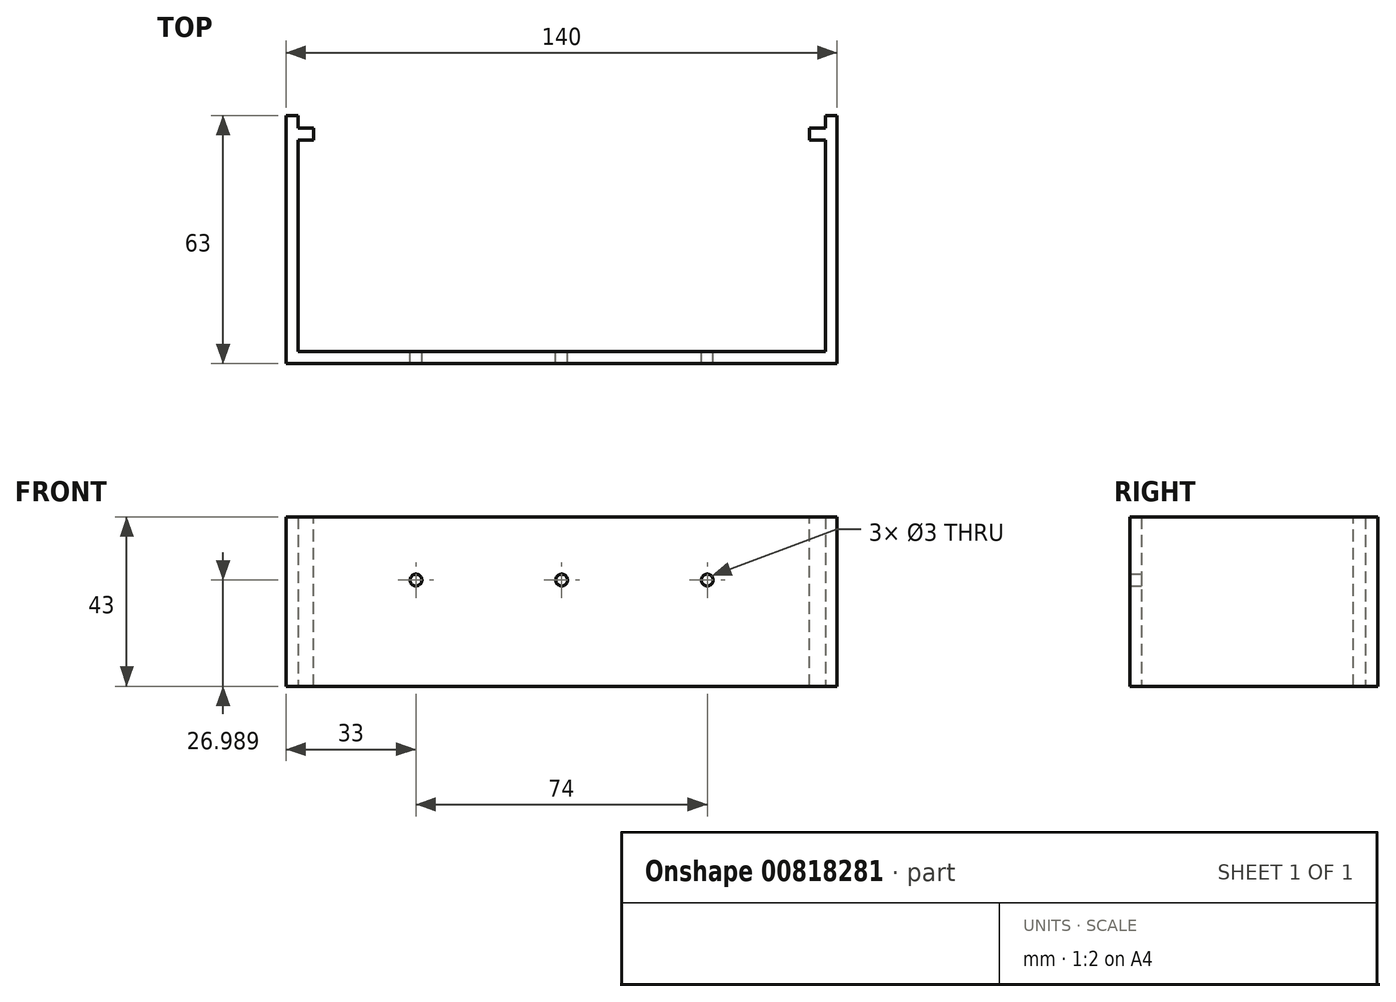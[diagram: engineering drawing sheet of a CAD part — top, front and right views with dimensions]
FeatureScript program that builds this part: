
annotation { "Feature Type Name" : "Feature", "Feature Type Description" : "" }
export const myFeature = defineFeature(function(context is Context, id is Id, definition is map)
    precondition{}
    {
        {
            var Q0;
            Q0=qCreatedBy(makeId("Top.planeOp"),FACE);
            var sketch = newSketch(context, id + "F0", { "sketchPlane" : qUnion([Q0])});
            skLineSegment(sketch, "E0.bottom", {"start": v(-80, 33.03) * mm, "end": v(60, 33.03) * mm});
            skLineSegment(sketch, "E0.top", {"start": v(-80, -32.97) * mm, "end": v(60, -32.97) * mm});
            skLineSegment(sketch, "E0.left", {"start": v(-80, 33.03) * mm, "end": v(-80, -32.97) * mm});
            skLineSegment(sketch, "E0.right", {"start": v(60, 33.03) * mm, "end": v(60, -32.97) * mm});
            skLineSegment(sketch, "E1.left", {"start": v(-80, -32.97) * mm, "end": v(-80, 0.03) * mm});
            skLineSegment(sketch, "E1.right", {"start": v(60, -9.97) * mm, "end": v(60, 0.03) * mm});
            skLineSegment(sketch, "E2.bottom", {"start": v(-80, -32.97) * mm, "end": v(-45, -32.97) * mm});
            skLineSegment(sketch, "E2.top", {"start": v(-80, 33.03) * mm, "end": v(-60, 33.03) * mm});
            skLineSegment(sketch, "E2.left", {"start": v(-80, -32.97) * mm, "end": v(-80, 33.03) * mm});
            skLineSegment(sketch, "E3.bottom", {"start": v(-45, -32.97) * mm, "end": v(-25, -32.97) * mm});
            skLineSegment(sketch, "E3.top", {"start": v(-60, 33.03) * mm, "end": v(-40, 33.03) * mm});
            skLineSegment(sketch, "E4.bottom", {"start": v(-25, -32.97) * mm, "end": v(-5, -32.97) * mm});
            skLineSegment(sketch, "E4.top", {"start": v(-40, 33.03) * mm, "end": v(-20, 33.03) * mm});
            skPoint(sketch, "E5.oppositeSnap0", {"position": v(-10, 33.03) * mm});
            skLineSegment(sketch, "E5.bottom", {"start": v(-5, -32.97) * mm, "end": v(15, -32.97) * mm});
            skLineSegment(sketch, "E5.top", {"start": v(-20, 33.03) * mm, "end": v(0, 33.03) * mm});
            skLineSegment(sketch, "E6.bottom", {"start": v(15, -32.97) * mm, "end": v(35, -32.97) * mm});
            skLineSegment(sketch, "E6.top", {"start": v(0, 33.03) * mm, "end": v(20, 33.03) * mm});
            skLineSegment(sketch, "E7.bottom", {"start": v(35, -32.97) * mm, "end": v(55, -32.97) * mm});
            skLineSegment(sketch, "E7.top", {"start": v(20, 33.03) * mm, "end": v(40, 33.03) * mm});
            skLineSegment(sketch, "E8.left", {"start": v(-80, -32.97) * mm, "end": v(-80, -2.97) * mm});
            skLineSegment(sketch, "E8.right", {"start": v(60, -24.97) * mm, "end": v(60, -4.97) * mm});
            skLineSegment(sketch, "E9.left", {"start": v(-80, 33.03) * mm, "end": v(-80, 18.03) * mm});
            skLineSegment(sketch, "E9.right", {"start": v(60, 33.03) * mm, "end": v(60, 18.03) * mm});
            skCircle(sketch, "E10", {"center": v(-45, 1.03) * mm, "radius": 8 * mm});
            skCircle(sketch, "E11", {"center": v(25, -0.47) * mm, "radius": 8 * mm});
            skLineSegment(sketch, "E12.left", {"start": v(-80, -32.97) * mm, "end": v(-80, -17.97) * mm});
            skLineSegment(sketch, "E12.right", {"start": v(60, -32.97) * mm, "end": v(60, -14.97) * mm});
            skLineSegment(sketch, "E13.top", {"start": v(-80, -29.97) * mm, "end": v(60, -29.97) * mm});
            skLineSegment(sketch, "E13.left", {"start": v(-80, -32.97) * mm, "end": v(-80, -29.97) * mm});
            skLineSegment(sketch, "E13.right", {"start": v(60, -32.97) * mm, "end": v(60, -29.97) * mm});
            skSolve(sketch);
        }
        {
            var Q0;
            Q0=makeQuery(id+"F0.imprint","IMPRINT",FACE,{"disambiguationData":[TD([[makeQuery(id+"F0.imprint","IMPRINT",EDGE,{"derivedFrom":sQuery(id+"F0.wireOp",EDGE,"E0.right")}),-1.0]])]});
            extrude(context, id + "F1", {"entities" : qUnion([Q0]), "depth" : 3 * mm, "offsetDistance" : 25 * mm});
        }
        {
            var Q0;
            Q0=makeQuery(id+"F1.opExtrude","CAP_FACE",FACE,{"disambiguationData":[OSD([sQuery(id+"F0.wireOp",EDGE,"E0.right"),sQuery(id+"F0.wireOp",EDGE,"E1.right"),sQuery(id+"F0.wireOp",EDGE,"E2.left"),sQuery(id+"F0.wireOp",EDGE,"E8.left"),sQuery(id+"F0.wireOp",EDGE,"E8.right"),sQuery(id+"F0.wireOp",EDGE,"E0.bottom"),sQuery(id+"F0.wireOp",EDGE,"E9.left"),sQuery(id+"F0.wireOp",EDGE,"E9.right"),sQuery(id+"F0.wireOp",EDGE,"l78r6zbi-zdNL-ogfi-jeJ1-84AOC1EXPDmI"),sQuery(id+"F0.wireOp",EDGE,"7xFXzIXv-dOzj-SHI9-m5NP-5MGqcVb28G0k"),sQuery(id+"F0.wireOp",EDGE,"E10"),sQuery(id+"F0.wireOp",EDGE,"k8Uu2vQ0-tXef-bBox-vRSx-lKBiwxJhI1xb"),sQuery(id+"F0.wireOp",EDGE,"E11"),sQuery(id+"F0.wireOp",EDGE,"5OqNOj1d-C8S8-WuIc-Ppvz-3VOTpNMQOR2k"),sQuery(id+"F0.wireOp",EDGE,"E12.left"),sQuery(id+"F0.wireOp",EDGE,"E12.right"),sQuery(id+"F0.wireOp",EDGE,"HoM0chx2-d7kJ-X9MT-WdqG-gqhH9dmnozYe"),sQuery(id+"F0.wireOp",EDGE,"JgkcrWLJ-2lYI-B5tP-8zwM-9y0SQbQCKJUD"),sQuery(id+"F0.wireOp",EDGE,"uQcqgJcq-6ofs-f9DD-1k3D-WOd607GN4n9v"),sQuery(id+"F0.wireOp",EDGE,"E13.top")])],"isStart":false});
            var sketch = newSketch(context, id + "F2", { "sketchPlane" : qUnion([Q0])});
            skLineSegment(sketch, "E14.bottom", {"start": v(-80, -29.97) * mm, "end": v(60, -29.97) * mm});
            skLineSegment(sketch, "E14.top", {"start": v(-80, -26.97) * mm, "end": v(60, -26.97) * mm});
            skLineSegment(sketch, "E14.left", {"start": v(-80, -29.97) * mm, "end": v(-80, -26.97) * mm});
            skLineSegment(sketch, "E14.right", {"start": v(60, -29.97) * mm, "end": v(60, -26.97) * mm});
            skLineSegment(sketch, "E15.left", {"start": v(-80, 33.03) * mm, "end": v(-80, 30.03) * mm});
            skLineSegment(sketch, "E15.right", {"start": v(60, 33.03) * mm, "end": v(60, 30.03) * mm});
            skLineSegment(sketch, "E16.bottom", {"start": v(-80, 33.03) * mm, "end": v(-77, 33.03) * mm});
            skLineSegment(sketch, "E16.top", {"start": v(-80, -29.97) * mm, "end": v(-77, -29.97) * mm});
            skLineSegment(sketch, "E16.left", {"start": v(-80, 33.03) * mm, "end": v(-80, -29.97) * mm});
            skLineSegment(sketch, "E16.right", {"start": v(-77, 33.03) * mm, "end": v(-77, -29.97) * mm});
            skLineSegment(sketch, "E17.bottom", {"start": v(60, 33.03) * mm, "end": v(57, 33.03) * mm});
            skLineSegment(sketch, "E17.top", {"start": v(60, -29.97) * mm, "end": v(57, -29.97) * mm});
            skLineSegment(sketch, "E17.left", {"start": v(60, 33.03) * mm, "end": v(60, -29.97) * mm});
            skLineSegment(sketch, "E17.right", {"start": v(57, 33.03) * mm, "end": v(57, -29.97) * mm});
            skSolve(sketch);
        }
        {
            var Q0;
            Q0=qSketchRegion(id+"F2",true);
            extrude(context, id + "F3", {"entities" : qUnion([Q0]), "operationType" : NewBodyOperationType.ADD, "depth" : 40 * mm, "offsetDistance" : 25 * mm});
        }
        {
            var Q0;
            Q0=makeQuery(id+"F3.opExtrude","SWEPT_FACE",FACE,{"disambiguationData":[OSD([sQuery(id+"F2.wireOp",EDGE,"E16.right")])]});
            var sketch = newSketch(context, id + "F4", { "sketchPlane" : qUnion([Q0])});
            skLineSegment(sketch, "E18.bottom", {"start": v(33.03, 43) * mm, "end": v(29.83, 43) * mm});
            skLineSegment(sketch, "E18.top", {"start": v(33.03, 3) * mm, "end": v(29.83, 3) * mm});
            skLineSegment(sketch, "E18.left", {"start": v(33.03, 43) * mm, "end": v(33.03, 3) * mm});
            skLineSegment(sketch, "E18.right", {"start": v(29.83, 43) * mm, "end": v(29.83, 3) * mm});
            skLineSegment(sketch, "E19.bottom", {"start": v(29.83, 43) * mm, "end": v(26.83, 43) * mm});
            skLineSegment(sketch, "E19.top", {"start": v(29.83, 3) * mm, "end": v(26.83, 3) * mm});
            skLineSegment(sketch, "E19.right", {"start": v(26.83, 43) * mm, "end": v(26.83, 3) * mm});
            skSolve(sketch);
        }
        {
            var Q0;
            Q0=makeQuery(id+"F4.imprint","IMPRINT",FACE,{"disambiguationData":[TD([[makeQuery(id+"F4.imprint","IMPRINT",EDGE,{"derivedFrom":sQuery(id+"F4.wireOp",EDGE,"E19.bottom")}),1.0]])]});
            extrude(context, id + "F5", {"entities" : qUnion([Q0]), "operationType" : NewBodyOperationType.ADD, "depth" : 134 * mm, "offsetDistance" : 25 * mm});
        }
        {
            var Q0;
            Q0=makeQuery(id+"F5.boolean.opBoolean","MERGE",FACE,{"derivedFrom":[makeQuery(id+"F3.opExtrude","CAP_FACE",FACE,{"disambiguationData":[OSD([sQuery(id+"F2.wireOp",EDGE,"E14.bottom"),sQuery(id+"F2.wireOp",EDGE,"E14.top"),sQuery(id+"F2.wireOp",EDGE,"E16.bottom"),sQuery(id+"F2.wireOp",EDGE,"E16.top"),sQuery(id+"F2.wireOp",EDGE,"E16.left"),sQuery(id+"F2.wireOp",EDGE,"E16.right"),sQuery(id+"F2.wireOp",EDGE,"E17.bottom"),sQuery(id+"F2.wireOp",EDGE,"E17.top"),sQuery(id+"F2.wireOp",EDGE,"E17.left"),sQuery(id+"F2.wireOp",EDGE,"E17.right")])],"isStart":false}),makeQuery(id+"F5.opExtrude","SWEPT_FACE",FACE,{"disambiguationData":[OSD([sQuery(id+"F4.wireOp",EDGE,"E19.bottom")])]})]});
            var sketch = newSketch(context, id + "F6", { "sketchPlane" : qUnion([Q0])});
            skLineSegment(sketch, "E20.bottom", {"start": v(-73, 29.83) * mm, "end": v(53, 29.83) * mm});
            skLineSegment(sketch, "E20.top", {"start": v(-73, 26.83) * mm, "end": v(53, 26.83) * mm});
            skLineSegment(sketch, "E20.left", {"start": v(-73, 29.83) * mm, "end": v(-73, 26.83) * mm});
            skLineSegment(sketch, "E20.right", {"start": v(53, 29.83) * mm, "end": v(53, 26.83) * mm});
            skSolve(sketch);
        }
        {
            var Q0;
            Q0=qSketchRegion(id+"F6",true);
            extrude(context, id + "F7", {"entities" : qUnion([Q0]), "operationType" : NewBodyOperationType.REMOVE, "oppositeDirection" : true, "depth" : 40 * mm, "offsetDistance" : 25 * mm});
        }
        {
            var Q0;
            Q0=makeQuery(id+"F3.opExtrude","SWEPT_FACE",FACE,{"disambiguationData":[OSD([sQuery(id+"F2.wireOp",EDGE,"E14.top")])]});
            var sketch = newSketch(context, id + "F8", { "sketchPlane" : qUnion([Q0])});
            skLineSegment(sketch, "E21.bottom", {"start": v(77, 43) * mm, "end": v(-57, 43) * mm});
            skLineSegment(sketch, "E21.left", {"start": v(77, 43) * mm, "end": v(77, 26.99) * mm});
            skLineSegment(sketch, "E21.right", {"start": v(-57, 43) * mm, "end": v(-57, 26.99) * mm});
            skCircle(sketch, "E22", {"center": v(47, 26.99) * mm, "radius": 1.5 * mm});
            skCircle(sketch, "E23", {"center": v(-27, 26.99) * mm, "radius": 1.5 * mm});
            skCircle(sketch, "E24", {"center": v(10, 26.99) * mm, "radius": 1.5 * mm});
            skSolve(sketch);
        }
        {
            var Q0;
            Q0=makeQuery(id+"F8.imprint","IMPRINT",FACE,{"disambiguationData":[TD([[makeQuery(id+"F8.imprint","IMPRINT",EDGE,{"derivedFrom":sQuery(id+"F8.wireOp",EDGE,"E22")}),1.0]])]});
            var Q1;
            Q1=makeQuery(id+"F8.imprint","IMPRINT",FACE,{"disambiguationData":[TD([[makeQuery(id+"F8.imprint","IMPRINT",EDGE,{"derivedFrom":sQuery(id+"F8.wireOp",EDGE,"E23")}),1.0]])]});
            var Q2;
            Q2=makeQuery(id+"F8.imprint","IMPRINT",FACE,{"disambiguationData":[TD([[makeQuery(id+"F8.imprint","IMPRINT",EDGE,{"derivedFrom":sQuery(id+"F8.wireOp",EDGE,"E24")}),1.0]])]});
            extrude(context, id + "F9", {"entities" : qUnion([Q0, Q1, Q2]), "operationType" : NewBodyOperationType.REMOVE, "oppositeDirection" : true, "depth" : 3 * mm, "offsetDistance" : 25 * mm});
        }
        {
            var Q0;
            {var subQ1=sQuery(id+"F0.wireOp",EDGE,"E0.bottom");var subQ3=sQuery(id+"F0.wireOp",EDGE,"E11");var subQ4=sQuery(id+"F0.wireOp",EDGE,"E10");var subQ5=makeQuery(id+"F1.opExtrude","CAP_FACE",FACE,{"disambiguationData":[OSD([sQuery(id+"F0.wireOp",EDGE,"E0.right"),sQuery(id+"F0.wireOp",EDGE,"E1.right"),sQuery(id+"F0.wireOp",EDGE,"E2.left"),sQuery(id+"F0.wireOp",EDGE,"E8.left"),sQuery(id+"F0.wireOp",EDGE,"E8.right"),subQ1,sQuery(id+"F0.wireOp",EDGE,"E9.left"),sQuery(id+"F0.wireOp",EDGE,"E9.right"),subQ4,subQ3,sQuery(id+"F0.wireOp",EDGE,"E12.left"),sQuery(id+"F0.wireOp",EDGE,"E12.right"),sQuery(id+"F0.wireOp",EDGE,"E13.top")])],"isStart":false});Q0=makeQuery(id+"F7.boolean.opBoolean","MERGE",FACE,{"derivedFrom":[makeQuery(id+"F5.boolean.opBoolean","SPLIT",FACE,{"disambiguationData":[TD([makeQuery(id+"F1.opExtrude","SWEPT_FACE",FACE,{"disambiguationData":[OSD([subQ4])]})])],"derivedFrom":subQ5}),makeQuery(id+"F5.boolean.opBoolean","SPLIT",FACE,{"disambiguationData":[TD([makeQuery(id+"F1.opExtrude","SWEPT_FACE",FACE,{"disambiguationData":[OSD([subQ1])]})])],"derivedFrom":subQ5}),makeQuery(id+"F7.opExtrude","CAP_FACE",FACE,{"disambiguationData":[OSD([sQuery(id+"F6.wireOp",EDGE,"E20.bottom"),sQuery(id+"F6.wireOp",EDGE,"E20.top"),sQuery(id+"F6.wireOp",EDGE,"E20.left"),sQuery(id+"F6.wireOp",EDGE,"E20.right")])],"isStart":false})]});}
            var sketch = newSketch(context, id + "F10", { "sketchPlane" : qUnion([Q0])});
            skSolve(sketch);
        }
        {
            var Q0;
            {var subQ3=sQuery(id+"F0.wireOp",EDGE,"E10");Q0=makeQuery(id+"F10.imprint","IMPRINT",FACE,{"disambiguationData":[TD([[makeQuery(id+"F10.imprint","IMPRINT",EDGE,{"derivedFrom":makeQuery(id+"F1.opExtrude","CAP_EDGE",EDGE,{"disambiguationData":[OSD([subQ3])],"isStart":false})}),-1.0]])]});}
            var sketch = newSketch(context, id + "F11", { "sketchPlane" : qUnion([Q0])});
            skSolve(sketch);
        }
        {
            var Q0;
            Q0 = qSketchRegion(id + "F11", true);
            var Q1;
            {var subQ3=sQuery(id+"F0.wireOp",EDGE,"E10");Q1=makeQuery(id+"F10.imprint","IMPRINT",FACE,{"disambiguationData":[TD([[makeQuery(id+"F10.imprint","IMPRINT",EDGE,{"derivedFrom":makeQuery(id+"F1.opExtrude","CAP_EDGE",EDGE,{"disambiguationData":[OSD([subQ3])],"isStart":false})}),-1.0]])]});}
            extrude(context, id + "F12", {"entities" : qUnion([Q0, Q1]), "operationType" : NewBodyOperationType.REMOVE, "oppositeDirection" : true, "depth" : 40 * mm, "offsetDistance" : 25 * mm});
        }
    });
